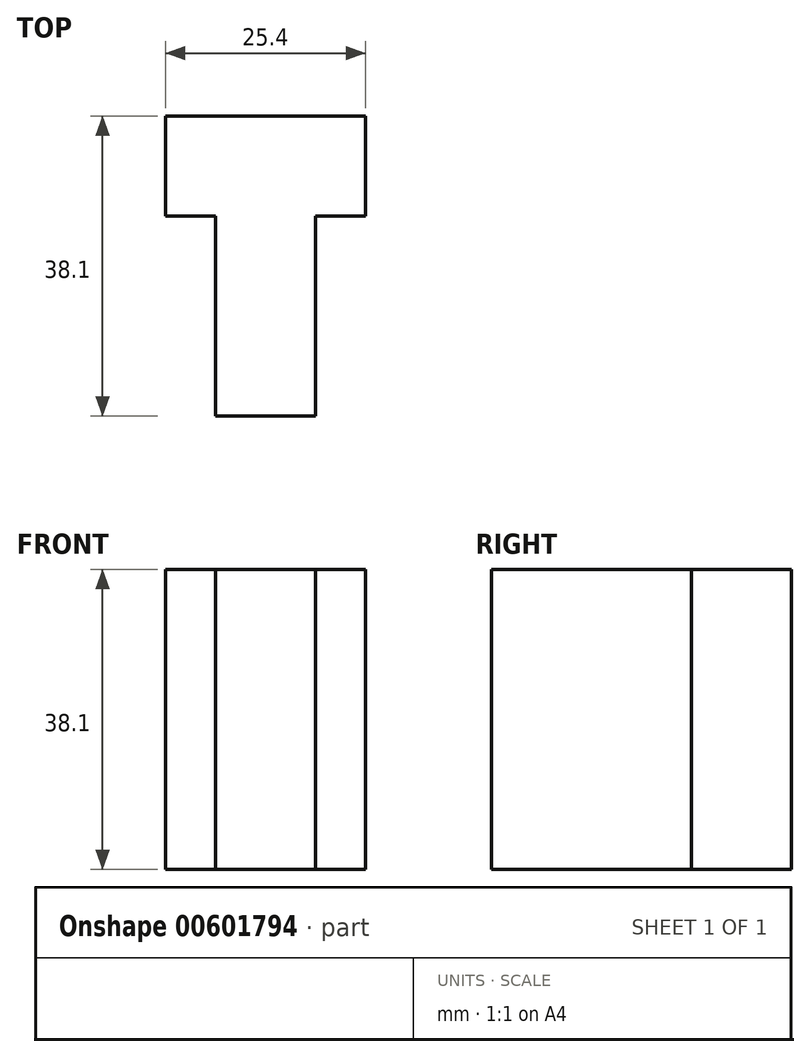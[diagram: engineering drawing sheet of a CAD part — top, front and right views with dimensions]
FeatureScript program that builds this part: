
annotation { "Feature Type Name" : "Feature", "Feature Type Description" : "" }
export const myFeature = defineFeature(function(context is Context, id is Id, definition is map)
    precondition{}
    {
        {
            var Q0;
            Q0=qCreatedBy(makeId("Top.planeOp"),FACE);
            var sketch = newSketch(context, id + "F0", { "sketchPlane" : qUnion([Q0])});
            skLineSegment(sketch, "E0", {"start": v(0, 0) * mm, "end": v(-6.35, 0) * mm});
            skLineSegment(sketch, "E1", {"start": v(-6.35, 0) * mm, "end": v(-6.35, -12.7) * mm});
            skLineSegment(sketch, "E2", {"start": v(-6.35, -12.7) * mm, "end": v(0, -12.7) * mm});
            skLineSegment(sketch, "E3", {"start": v(0, -12.7) * mm, "end": v(0, -38.1) * mm});
            skLineSegment(sketch, "E4", {"start": v(0, -38.1) * mm, "end": v(12.7, -38.1) * mm});
            skLineSegment(sketch, "E5", {"start": v(12.7, -38.1) * mm, "end": v(12.7, -12.7) * mm});
            skLineSegment(sketch, "E6", {"start": v(12.7, -12.7) * mm, "end": v(19.05, -12.7) * mm});
            skLineSegment(sketch, "E7", {"start": v(19.05, -12.7) * mm, "end": v(19.05, 0) * mm});
            skLineSegment(sketch, "E8", {"start": v(19.05, 0) * mm, "end": v(0, 0) * mm});
            skSolve(sketch);
        }
        {
            var Q0;
            Q0=makeQuery(id+"F0.imprint","IMPRINT",FACE,{"disambiguationData":[TD([[makeQuery(id+"F0.imprint","IMPRINT",EDGE,{"derivedFrom":sQuery(id+"F0.wireOp",EDGE,"E0")}),1.0]])]});
            extrude(context, id + "F1", {"entities" : qUnion([Q0]), "depth" : 38.1 * mm, "offsetDistance" : 25.4 * mm});
        }
    });
